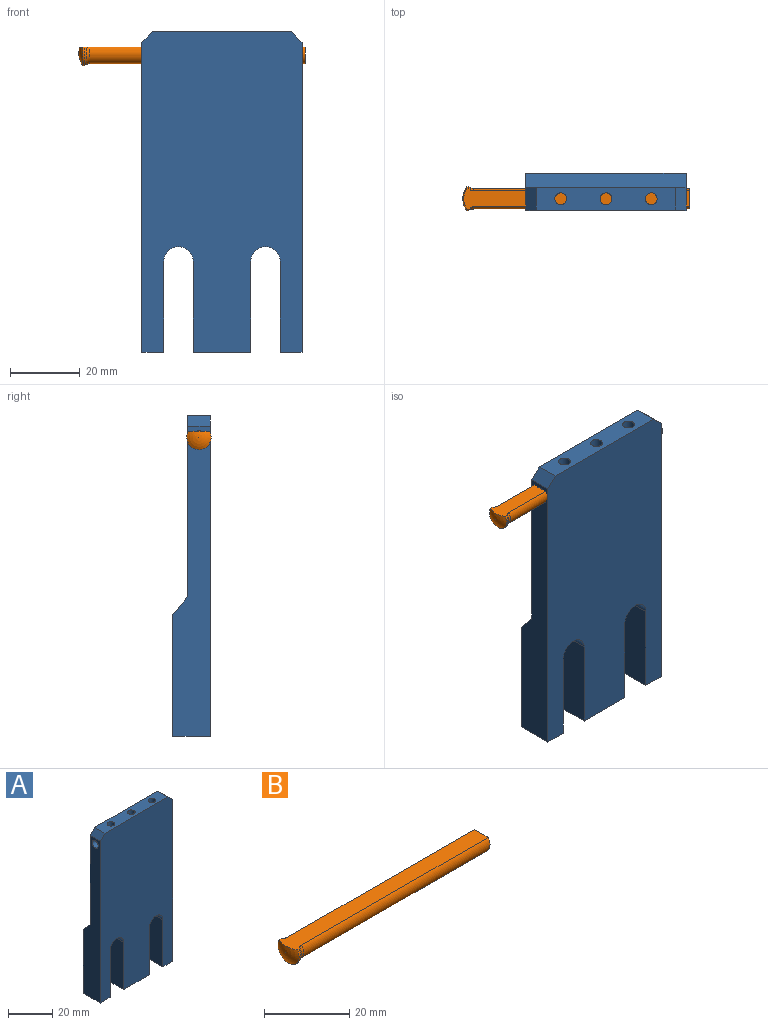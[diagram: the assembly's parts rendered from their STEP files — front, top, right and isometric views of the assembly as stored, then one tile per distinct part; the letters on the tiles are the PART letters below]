
ASSEMBLY  parts=2 mates=1
PART A: 75 faces, bbox 46x10.8x92 mm
  f0: plane 52x46mm, normal (0,1,0), area 2323.1mm2, adj f12,f13,f14,f19,f20,f21,f36,f37
  f1: plane 10.75x6.25mm, normal (0,0,-1), area 67.2mm2, adj f3,f5,f14,f15
  f2: plane 16.5x10.75mm, normal (0,0,-1), area 177.4mm2, adj f3,f7,f8,f15
  f3: plane 46x35mm, normal (0,1,0), area 1111.3mm2, adj f1,f2,f5,f6,f7,f8,f9,f10
  f4: cylinder r=1.95mm len=46mm, axis (-1,0,0), area 532.5mm2, adj f12,f14,f16,f17,f18
  f5: plane 26x10.75mm, normal (1,0,0), area 279.5mm2, adj f1,f3,f6,f15
  f6: cylinder r=4.25mm len=10.75mm, axis (0,1,0), area 143.5mm2, adj f3,f5,f7,f15
  f7: plane 26x10.75mm, normal (-1,0,0), area 279.5mm2, adj f2,f3,f6,f15
  f8: plane 26x10.75mm, normal (1,0,0), area 279.5mm2, adj f2,f3,f9,f15
  f9: cylinder r=4.25mm len=10.75mm, axis (0,1,0), area 143.5mm2, adj f3,f8,f10,f15
  f10: plane 26x10.75mm, normal (-1,0,0), area 279.5mm2, adj f3,f9,f11,f15
  f11: plane 10.75x6.25mm, normal (0,0,-1), area 67.2mm2, adj f3,f10,f12,f15
  f12: plane 89x10.75mm, normal (1,0,0), area 725.9mm2, adj f0,f3,f4,f11,f15,f19,f20
  f13: plane 40x6.5mm, normal (0,0,1), area 232.8mm2, adj f0,f15,f16,f17,f18,f20,f21
  f14: plane 89x10.75mm, normal (-1,0,0), area 725.9mm2, adj f0,f1,f3,f4,f15,f19,f21
  f15: plane 92x46mm, normal (0,-1,0), area 3724.3mm2, adj f1,f2,f5,f6,f7,f8,f9,f10
  f16: cylinder r=1.7mm len=5.25mm, axis (0,0,1), area 50.2mm2, adj f4,f13
  f17: cylinder r=1.7mm len=5.25mm, axis (0,0,1), area 50.2mm2, adj f4,f13
  f18: cylinder r=1.7mm len=5.25mm, axis (0,0,1), area 50.2mm2, adj f4,f13
  f19: plane 46x5mm, normal (0,0.76,0.65), area 301.9mm2, adj f0,f3,f12,f14
  f20: plane 6.5x3mm, normal (0.71,0,0.71), area 27.6mm2, adj f0,f12,f13,f15
  f21: plane 6.5x3mm, normal (-0.71,0,0.71), area 27.6mm2, adj f0,f13,f14,f15
  f22: extruded ~1.06x0.33mm, area 0.3mm2, adj f23,f52,f53,f74
  f23: extruded ~1.08x0.32mm, area 0.3mm2, adj f22,f24,f53,f74
  f24: extruded ~0.87x0.39mm, area 0.3mm2, adj f23,f25,f53,f74
  f25: extruded ~0.87x0.32mm, area 0.3mm2, adj f24,f26,f53,f74
  f26: extruded ~1.1x0.7mm, area 0.4mm2, adj f25,f27,f53,f74
  f27: extruded ~1.18x0.72mm, area 0.4mm2, adj f26,f28,f53,f74
  f28: extruded ~0.86x0.32mm, area 0.3mm2, adj f27,f52,f53,f74
  f29: extruded ~1.01x0.45mm, area 0.3mm2, adj f30,f50,f53,f54
  f30: extruded ~1.01x0.36mm, area 0.3mm2, adj f29,f31,f53,f54
  f31: extruded ~1.17x0.77mm, area 0.4mm2, adj f30,f32,f53,f54
  f32: extruded ~1.48x0.8mm, area 0.5mm2, adj f31,f33,f53,f54
  f33: extruded ~0.94x0.42mm, area 0.3mm2, adj f32,f34,f53,f54
  f34: extruded ~1.04x0.45mm, area 0.4mm2, adj f33,f35,f53,f54
  f35: extruded ~1.26x0.38mm, area 0.4mm2, adj f34,f50,f53,f54
  f36: extruded ~1.72x0.5mm, area 0.5mm2, adj f0,f37,f51,f53
  f37: extruded ~1.71x0.51mm, area 0.5mm2, adj f0,f36,f38,f53
  f38: extruded ~1.38x0.64mm, area 0.5mm2, adj f0,f37,f39,f53
  f39: extruded ~1.1x0.33mm, area 0.3mm2, adj f0,f38,f40,f53
  f40: extruded ~1.07x0.91mm, area 0.4mm2, adj f0,f39,f41,f53
  f41: extruded ~2.12x1.66mm, area 0.9mm2, adj f0,f40,f42,f53
  f42: extruded ~1.58x0.68mm, area 0.5mm2, adj f0,f41,f43,f53
  f43: extruded ~1.95x0.56mm, area 0.6mm2, adj f0,f42,f44,f53
  f44: extruded ~1.89x0.59mm, area 0.6mm2, adj f0,f43,f45,f53
  f45: extruded ~1.58x0.69mm, area 0.5mm2, adj f0,f44,f46,f53
  f46: extruded ~1.18x0.41mm, area 0.4mm2, adj f0,f45,f47,f53
  f47: extruded ~1.37x0.97mm, area 0.5mm2, adj f0,f46,f48,f53
  f48: extruded ~1.16x0.88mm, area 0.4mm2, adj f0,f47,f49,f53
  f49: extruded ~1.07x0.36mm, area 0.3mm2, adj f0,f48,f51,f53
  f50: extruded ~1.27x0.36mm, area 0.4mm2, adj f29,f35,f53,f54
  f51: extruded ~1.39x0.63mm, area 0.5mm2, adj f0,f36,f49,f53
  f52: extruded ~0.87x0.39mm, area 0.3mm2, adj f22,f28,f53,f74
  f53: plane 8.15x5.21mm, normal (0,1,0), area 18.6mm2, adj f22,f23,f24,f25,f26,f27,f28,f29
  f54: plane 3.43x3.15mm, normal (0,1,0), area 8.2mm2, adj f29,f30,f31,f32,f33,f34,f35,f50
  f55: plane 7.03x2.69mm, normal (-0.93,0,0.36), area 2.3mm2, adj f0,f56,f72,f73
  f56: plane 0.74x0.3mm, normal (0,0,1), area 0.2mm2, adj f0,f55,f57,f73
  f57: plane 7.02x2.71mm, normal (0.93,0,0.36), area 2.3mm2, adj f0,f56,f58,f73
  f58: plane 0.3x0.04mm, normal (0,0,1), area 0mm2, adj f0,f57,f59,f73
  f59: extruded ~1.91x0.3mm, area 0.6mm2, adj f0,f58,f60,f73
  f60: plane 5.11x0.3mm, normal (-1,0,0), area 1.5mm2, adj f0,f59,f61,f73
  f61: plane 0.92x0.3mm, normal (0,0,1), area 0.3mm2, adj f0,f60,f62,f73
  f62: plane 7.93x0.3mm, normal (1,0,0), area 2.4mm2, adj f0,f61,f63,f73
  f63: plane 1.38x0.3mm, normal (0,0,-1), area 0.4mm2, adj f0,f62,f64,f73
  f64: plane 6.54x2.53mm, normal (-0.93,0,-0.36), area 2.1mm2, adj f0,f63,f65,f73
  f65: plane 0.3x0.04mm, normal (0,0,-1), area 0mm2, adj f0,f64,f66,f73
  f66: plane 6.54x2.51mm, normal (0.93,0,-0.36), area 2.1mm2, adj f0,f65,f67,f73
  f67: plane 1.39x0.3mm, normal (0,0,-1), area 0.4mm2, adj f0,f66,f68,f73
  f68: plane 7.93x0.3mm, normal (-1,0,0), area 2.4mm2, adj f0,f67,f69,f73
  f69: plane 0.85x0.3mm, normal (0,0,1), area 0.3mm2, adj f0,f68,f70,f73
  f70: plane 5.05x0.3mm, normal (1,0,0), area 1.5mm2, adj f0,f69,f71,f73
  f71: extruded ~1.99x0.3mm, area 0.6mm2, adj f0,f70,f72,f73
  f72: plane 0.3x0.04mm, normal (0,0,1), area 0mm2, adj f0,f55,f71,f73
  f73: plane 7.93x7.86mm, normal (0,1,0), area 26.9mm2, adj f55,f56,f57,f58,f59,f60,f61,f62
  f74: plane 2.93x2.77mm, normal (0,1,0), area 6.1mm2, adj f22,f23,f24,f25,f26,f27,f28,f52
PART B: 7 faces, bbox 65.1x7.6x7.4 mm
  f0: cylinder r=3.5mm len=7mm, axis (-1,0,0), area 7.4mm2, adj f1,f5,f6
  f1: sphere r=6mm, area 34.2mm2, adj f0,f6
  f2: plane 5.82x4.71mm, normal (1,0,0), area 23.1mm2, adj f3,f6
  f3: cylinder r=2.91mm len=61.82mm, axis (-1,0,0), area 805.1mm2, adj f2,f4,f6
  f4: torus R=4.91mm, axis (-1,0,0), area 13.9mm2, adj f3,f5,f6
  f5: cone r=3.5mm half-angle=30deg, axis (-1,0,0), area 9.2mm2, adj f0,f4,f6
  f6: plane 64.81x6.09mm, normal (0,0,1), area 297.1mm2, adj f0,f1,f2,f3,f4,f5
PLACE A at identity fixed
PLACE B t=(-37.91,0,85.8)mm
MATE revolute B.f0 <-> A.f4  axis (-1,0,0) through (-7,0,85.8)mm
